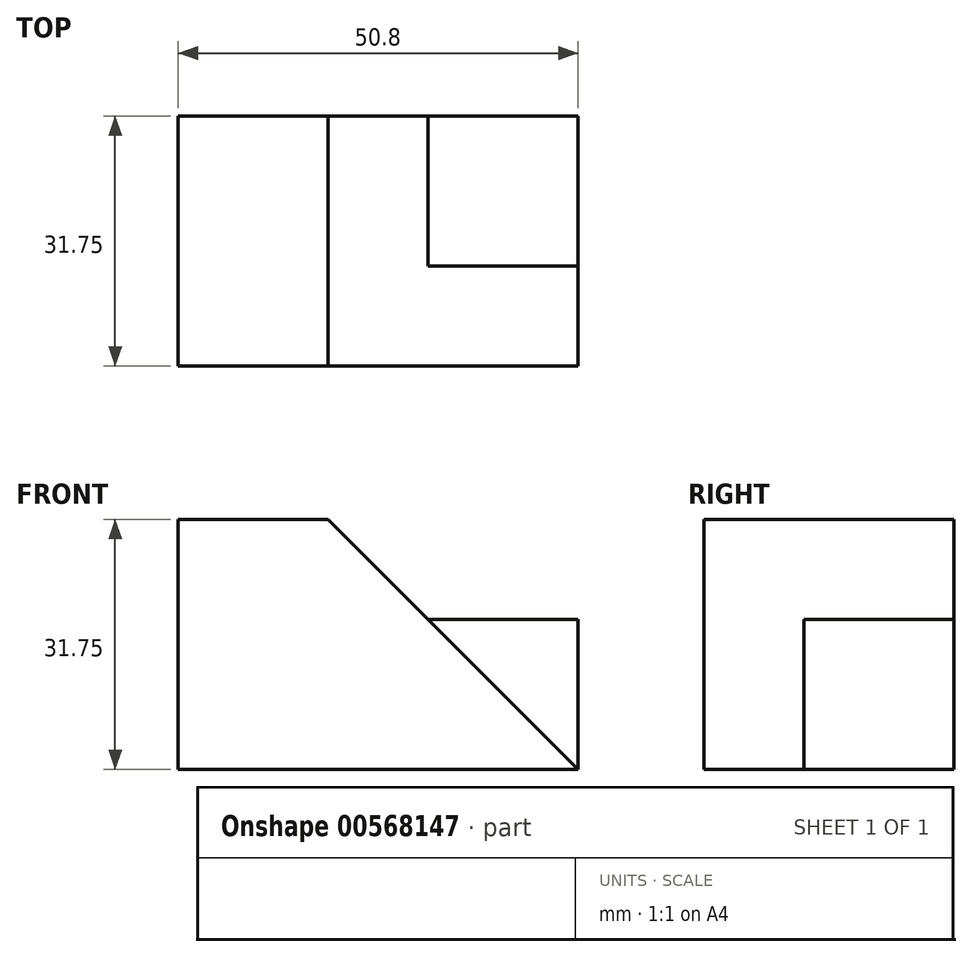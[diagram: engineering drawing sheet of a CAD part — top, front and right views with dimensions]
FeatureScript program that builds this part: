
annotation { "Feature Type Name" : "Feature", "Feature Type Description" : "" }
export const myFeature = defineFeature(function(context is Context, id is Id, definition is map)
    precondition{}
    {
        {
            var Q0;
            Q0=qCreatedBy(makeId("Front.planeOp"),FACE);
            var sketch = newSketch(context, id + "F0", { "sketchPlane" : qUnion([Q0])});
            skLineSegment(sketch, "E0", {"start": v(-66.5, 59.27) * mm, "end": v(-66.5, 27.52) * mm});
            skLineSegment(sketch, "E1", {"start": v(-66.5, 27.52) * mm, "end": v(-15.7, 27.52) * mm});
            skLineSegment(sketch, "E2", {"start": v(-15.7, 27.52) * mm, "end": v(-15.7, 59.27) * mm});
            skLineSegment(sketch, "E3", {"start": v(-15.7, 59.27) * mm, "end": v(-66.5, 59.27) * mm});
            skSolve(sketch);
        }
        {
            var Q0;
            Q0=makeQuery(id+"F0.imprint","IMPRINT",FACE,{"disambiguationData":[TD([[makeQuery(id+"F0.imprint","IMPRINT",EDGE,{"derivedFrom":sQuery(id+"F0.wireOp",EDGE,"E0")}),1.0]])]});
            extrude(context, id + "F1", {"entities" : qUnion([Q0]), "depth" : 31.75 * mm, "offsetDistance" : 25.4 * mm});
        }
        {
            var Q0;
            Q0=makeQuery(id+"F1.opExtrude","CAP_FACE",FACE,{"disambiguationData":[OSD([sQuery(id+"F0.wireOp",EDGE,"E0"),sQuery(id+"F0.wireOp",EDGE,"E1"),sQuery(id+"F0.wireOp",EDGE,"E2"),sQuery(id+"F0.wireOp",EDGE,"E3")])],"isStart":false});
            var sketch = newSketch(context, id + "F2", { "sketchPlane" : qUnion([Q0])});
            skLineSegment(sketch, "E4", {"start": v(-34.76, 59.27) * mm, "end": v(-34.76, 46.57) * mm});
            skLineSegment(sketch, "E5", {"start": v(-34.76, 46.57) * mm, "end": v(-15.7, 46.57) * mm});
            skSolve(sketch);
        }
        {
            var Q0;
            {var subQ0=sQuery(id+"F2.wireOp",EDGE,"E4");Q0=makeQuery(id+"F2.imprint","IMPRINT",FACE,{"disambiguationData":[TD([[makeQuery(id+"F2.imprint","IMPRINT",EDGE,{"derivedFrom":subQ0}),1.0]])]});}
            extrude(context, id + "F3", {"entities" : qUnion([Q0]), "operationType" : NewBodyOperationType.REMOVE, "oppositeDirection" : true, "depth" : 31.75 * mm, "offsetDistance" : 25.4 * mm});
        }
        {
            var Q0;
            Q0=makeQuery(id+"F1.opExtrude","CAP_FACE",FACE,{"disambiguationData":[OSD([sQuery(id+"F0.wireOp",EDGE,"E0"),sQuery(id+"F0.wireOp",EDGE,"E1"),sQuery(id+"F0.wireOp",EDGE,"E2"),sQuery(id+"F0.wireOp",EDGE,"E3")])],"isStart":false});
            var sketch = newSketch(context, id + "F4", { "sketchPlane" : qUnion([Q0])});
            skLineSegment(sketch, "E6", {"start": v(-34.76, 46.57) * mm, "end": v(-47.46, 59.27) * mm});
            skSolve(sketch);
        }
        {
            var Q0;
            {var subQ0=sQuery(id+"F4.wireOp",EDGE,"E6");Q0=makeQuery(id+"F4.imprint","IMPRINT",FACE,{"disambiguationData":[TD([[makeQuery(id+"F4.imprint","IMPRINT",EDGE,{"derivedFrom":subQ0}),-1.0]])]});}
            extrude(context, id + "F5", {"entities" : qUnion([Q0]), "operationType" : NewBodyOperationType.REMOVE, "oppositeDirection" : true, "depth" : 31.75 * mm, "offsetDistance" : 25.4 * mm});
        }
        {
            var Q0;
            Q0=makeQuery(id+"F1.opExtrude","CAP_FACE",FACE,{"disambiguationData":[OSD([sQuery(id+"F0.wireOp",EDGE,"E0"),sQuery(id+"F0.wireOp",EDGE,"E1"),sQuery(id+"F0.wireOp",EDGE,"E2"),sQuery(id+"F0.wireOp",EDGE,"E3")])],"isStart":false});
            var sketch = newSketch(context, id + "F6", { "sketchPlane" : qUnion([Q0])});
            skLineSegment(sketch, "E7", {"start": v(-34.76, 46.57) * mm, "end": v(-15.7, 27.52) * mm});
            skSolve(sketch);
        }
        {
            var Q0;
            Q0=makeQuery(id+"F6.imprint","IMPRINT",FACE,{"disambiguationData":[TD([[makeQuery(id+"F6.imprint","IMPRINT",EDGE,{"derivedFrom":sQuery(id+"F6.wireOp",EDGE,"E7")}),1.0]])]});
            extrude(context, id + "F7", {"entities" : qUnion([Q0]), "operationType" : NewBodyOperationType.REMOVE, "oppositeDirection" : true, "depth" : 12.7 * mm, "offsetDistance" : 25.4 * mm});
        }
    });
